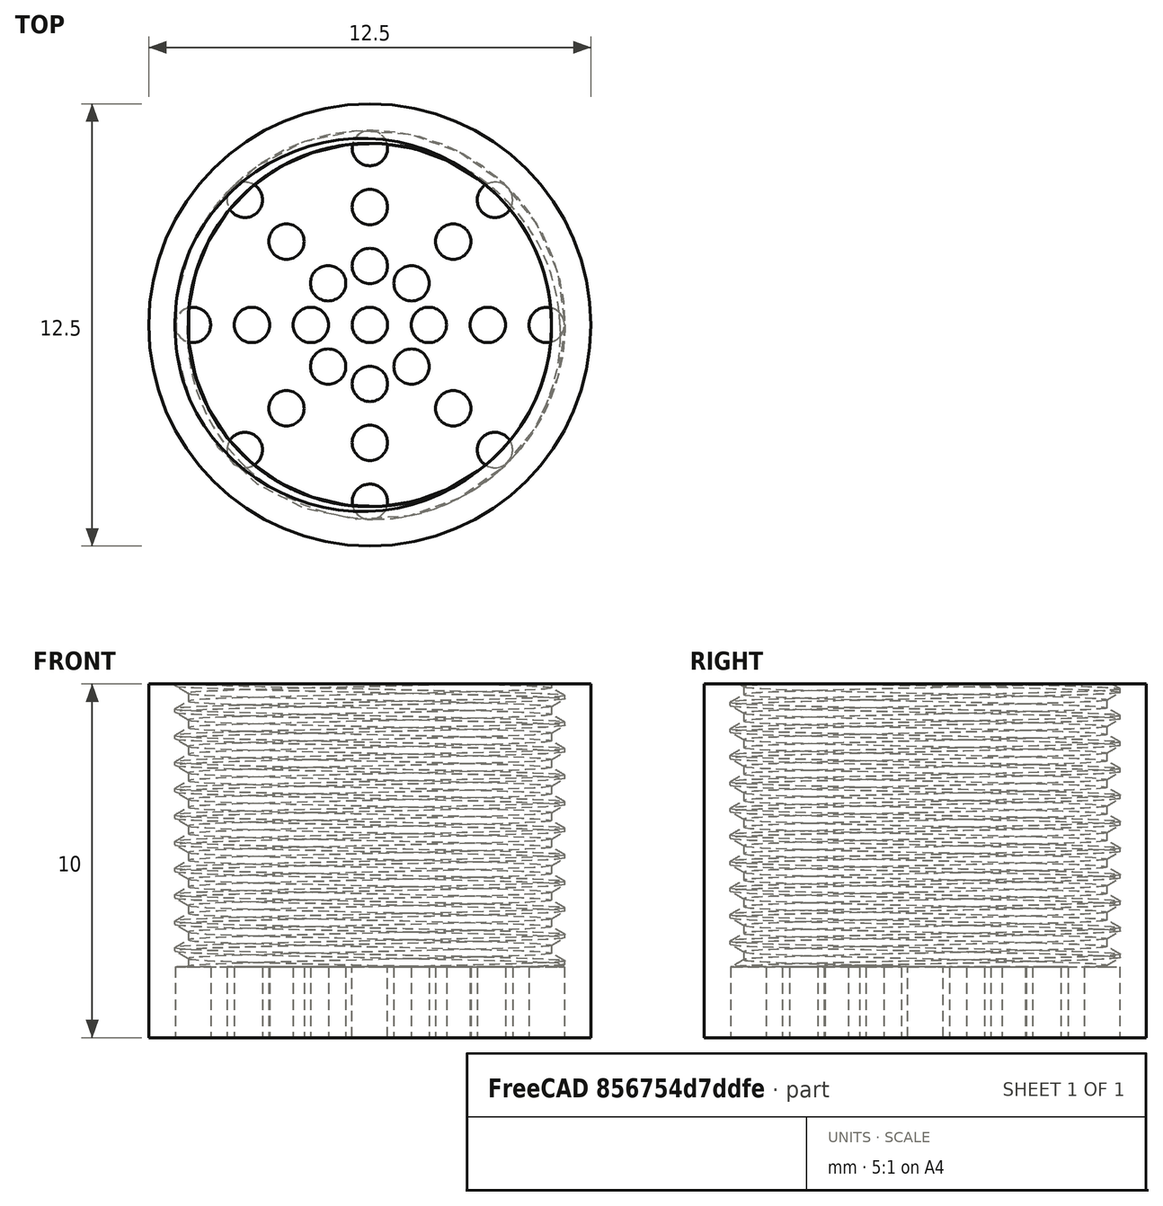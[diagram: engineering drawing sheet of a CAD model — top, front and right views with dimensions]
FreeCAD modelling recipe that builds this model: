
FCSTD DOCUMENT  (FreeCAD 0.21R33771 (Git))
Label: Tap
License: All rights reserved
LicenseURL: http://en.wikipedia.org/wiki/All_rights_reserved
objects: Sketcher::SketchObject×3, PartDesign::Pad×2, PartDesign::Hole×1, PartDesign::Pocket×1, PartDesign::LinearPattern×1, PartDesign::PolarPattern×1, PartDesign::MultiTransform×1, PartDesign::Body×1, Mesh::Feature×1
note: 15 computed .brp shape members not serialized (recipe doc carries the construction recipe); baked Part::Feature solids carry a one-line shape summary decoded from their .brp

FEATURE [Sketcher::SketchObject] Sketch
  FullyConstrained = true
  MapMode = 5
  Support = -> [XY_Plane]
  sketch-geometry (1):
    g0: Circle CenterX=0 CenterY=0 CenterZ=0 NormalX=0 NormalY=0 NormalZ=1 AngleXU=0 Radius=6.25
  constraints (2):
    c: Coincident(g0,g-1)
    c: Diameter(g0) = 12.5
FEATURE [PartDesign::Pad] Pad
  Direction = (0,0,1)
  Length = 8
  Length2 = 10
  Profile = -> Sketch
  ReferenceAxis = -> Sketch [N_Axis]
  Type = 0
FEATURE [PartDesign::Hole] Hole
  BaseFeature = -> Pad
  CustomThreadClearance = 0
  Depth = 25
  DepthType = 0
  Diameter = 10.272
  DrillForDepth = false
  DrillPoint = 1
  DrillPointAngle = 118
  HoleCutCountersinkAngle = 90
  HoleCutCustomValues = false
  HoleCutDepth = 0
  HoleCutDiameter = 0
  HoleCutType = 0
  ModelThread = true
  Profile = -> Pad [Face3]
  Tapered = false
  TaperedAngle = 90
  ThreadClass = 0
  ThreadDepth = 25
  ThreadDepthType = 0
  ThreadDirection = 0
  ThreadFit = 0
  ThreadSize = 24
  ThreadType = 2
  Threaded = true
  UseCustomThreadClearance = false
FEATURE [Sketcher::SketchObject] Sketch001
  FullyConstrained = true
  MapMode = 5
  Placement = pos=(0,0,0) rot=(1,0,0;3.14159rad)
  Support = -> [Hole]
  sketch-geometry (1):
    g0: Circle CenterX=0 CenterY=0 CenterZ=0 NormalX=0 NormalY=0 NormalZ=1 AngleXU=0 Radius=6.25
  constraints (2):
    c: Coincident(g0,g-1)
    c: Diameter(g0) = 12.5
FEATURE [PartDesign::Pad] Pad001
  BaseFeature = -> Hole
  Direction = (0,0,-1)
  Length = 2
  Length2 = 10
  Profile = -> Sketch001
  ReferenceAxis = -> Sketch001 [N_Axis]
  Type = 0
FEATURE [Sketcher::SketchObject] Sketch002
  FullyConstrained = true
  MapMode = 5
  Placement = pos=(0,0,-2) rot=(1,0,0;3.14159rad)
  Support = -> [Pad001]
  sketch-geometry (1):
    g0: Circle CenterX=0 CenterY=0 CenterZ=0 NormalX=0 NormalY=0 NormalZ=1 AngleXU=0 Radius=0.5
  constraints (2):
    c: Coincident(g0,g-1)
    c: Diameter(g0) = 1
FEATURE [PartDesign::Pocket] Pocket
  BaseFeature = -> Pad001
  Direction = (0,0,1)
  Length = 2
  Length2 = 5
  Profile = -> Sketch002
  ReferenceAxis = -> Sketch002 [N_Axis]
  Type = 0
FEATURE [PartDesign::LinearPattern] LinearPattern
  Direction = -> Y_Axis
  Length = 5
  Occurrences = 4
  Reversed = true
FEATURE [PartDesign::PolarPattern] PolarPattern
  Angle = 360
  Axis = -> Sketch002 [N_Axis]
  Occurrences = 8
FEATURE [PartDesign::MultiTransform] MultiTransform
  BaseFeature = -> Pocket
  Originals = -> [Pocket]
  Transformations = -> [LinearPattern,PolarPattern]
FEATURE [PartDesign::Body] Body
  Group = -> [Sketch,Pad,Hole,Sketch001,Pad001,Sketch002,Pocket,MultiTransform,LinearPattern,PolarPattern]
  Origin = -> Origin
  Tip = -> MultiTransform
FEATURE [Mesh::Feature] Mesh  label="Body (Meshed)"
